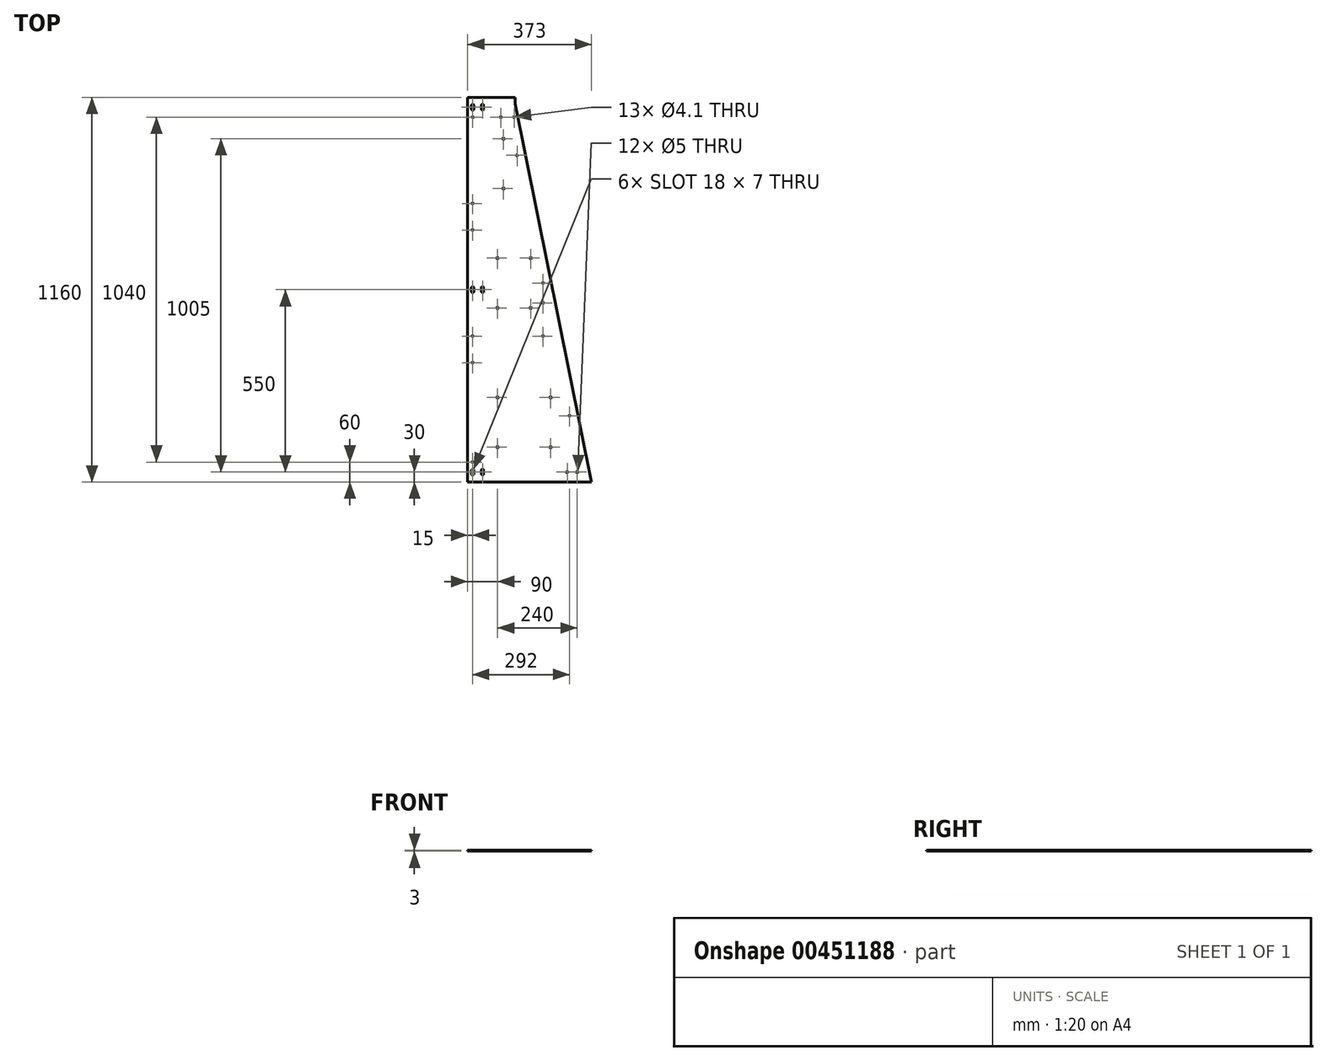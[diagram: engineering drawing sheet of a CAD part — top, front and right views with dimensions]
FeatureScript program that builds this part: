
annotation { "Feature Type Name" : "Feature", "Feature Type Description" : "" }
export const myFeature = defineFeature(function(context is Context, id is Id, definition is map)
    precondition{}
    {
        {
            var Q0;
            Q0=qCreatedBy(makeId("Top.planeOp"),FACE);
            var sketch = newSketch(context, id + "F0", { "sketchPlane" : qUnion([Q0])});
            skLineSegment(sketch, "E0", {"start": v(0, 0) * mm, "end": v(0, 1140) * mm});
            skLineSegment(sketch, "E1", {"start": v(0, 1140) * mm, "end": v(143, 1140) * mm});
            skLineSegment(sketch, "E2", {"start": v(143, 1140) * mm, "end": v(373, 0) * mm});
            skLineSegment(sketch, "E3", {"start": v(373, 0) * mm, "end": v(0, 0) * mm});
            skLineSegment(sketch, "E4", {"start": v(0, 1140) * mm, "end": v(0, 1160) * mm});
            skLineSegment(sketch, "E5", {"start": v(0, 1160) * mm, "end": v(143, 1160) * mm});
            skLineSegment(sketch, "E6", {"start": v(143, 1160) * mm, "end": v(143, 1140) * mm});
            skSolve(sketch);
        }
        {
            var Q0;
            Q0=qSketchRegion(id+"F0",true);
            extrude(context, id + "F1", {"entities" : qUnion([Q0]), "oppositeDirection" : true, "depth" : 3 * mm, "offsetDistance" : 25 * mm});
        }
        {
            var Q0;
            Q0=makeQuery(id+"F1.opExtrude","CAP_FACE",FACE,{"disambiguationData":[OSD([sQuery(id+"F0.wireOp",EDGE,"E0"),sQuery(id+"F0.wireOp",EDGE,"E1"),sQuery(id+"F0.wireOp",EDGE,"E2"),sQuery(id+"F0.wireOp",EDGE,"E3")])],"isStart":true});
            var sketch = newSketch(context, id + "F2", { "sketchPlane" : qUnion([Q0])});
            skCircle(sketch, "E7", {"center": v(90, 105) * mm, "radius": 2.5 * mm});
            skCircle(sketch, "E8", {"center": v(250, 105) * mm, "radius": 2.5 * mm});
            skCircle(sketch, "E9", {"center": v(250, 255) * mm, "radius": 2.5 * mm});
            skCircle(sketch, "E10", {"center": v(90, 255) * mm, "radius": 2.5 * mm});
            skCircle(sketch, "E11", {"center": v(90, 525) * mm, "radius": 2.5 * mm});
            skCircle(sketch, "E12", {"center": v(90, 675) * mm, "radius": 2.5 * mm});
            skCircle(sketch, "E13", {"center": v(190, 525) * mm, "radius": 2.5 * mm});
            skCircle(sketch, "E14", {"center": v(190, 675) * mm, "radius": 2.5 * mm});
            skCircle(sketch, "E15", {"center": v(108, 885) * mm, "radius": 2.5 * mm});
            skCircle(sketch, "E16", {"center": v(108, 1035) * mm, "radius": 2.5 * mm});
            skCircle(sketch, "E17", {"center": v(330, 30) * mm, "radius": 2.5 * mm});
            skCircle(sketch, "E18", {"center": v(300, 30) * mm, "radius": 2.5 * mm});
            skSolve(sketch);
        }
        {
            var Q0;
            Q0=qSketchRegion(id+"F2",true);
            extrude(context, id + "F3", {"entities" : qUnion([Q0]), "operationType" : NewBodyOperationType.REMOVE, "oppositeDirection" : true, "depth" : 25 * mm, "offsetDistance" : 25 * mm});
        }
        {
            var Q0;
            Q0=makeQuery(id+"F1.opExtrude","CAP_FACE",FACE,{"disambiguationData":[OSD([sQuery(id+"F0.wireOp",EDGE,"E0"),sQuery(id+"F0.wireOp",EDGE,"E1"),sQuery(id+"F0.wireOp",EDGE,"E2"),sQuery(id+"F0.wireOp",EDGE,"E3")])],"isStart":true});
            var sketch = newSketch(context, id + "F4", { "sketchPlane" : qUnion([Q0])});
            skLineSegment(sketch, "E19.bottom", {"start": v(18.5, 24.5) * mm, "end": v(11.5, 24.5) * mm, "construction": true});
            skLineSegment(sketch, "E19.top", {"start": v(18.5, 35.5) * mm, "end": v(11.5, 35.5) * mm, "construction": true});
            skLineSegment(sketch, "E19.left", {"start": v(18.5, 24.5) * mm, "end": v(18.5, 35.5) * mm});
            skLineSegment(sketch, "E19.right", {"start": v(11.5, 24.5) * mm, "end": v(11.5, 35.5) * mm});
            skPoint(sketch, "E19.middle", {"position": v(15, 30) * mm});
            skArc(sketch, "E20", {"start": v(18.5, 35.5) * mm, "mid": v(15, 39) * mm, "end": v(11.5, 35.5) * mm});
            skArc(sketch, "E21", {"start": v(11.5, 24.5) * mm, "mid": v(15, 21) * mm, "end": v(18.5, 24.5) * mm});
            skLineSegment(sketch, "E22", {"start": v(81.14, 580) * mm, "end": v(105.06, 580) * mm, "construction": true});
            skLineSegment(sketch, "E23.bottom", {"start": v(48.5, 24.5) * mm, "end": v(41.5, 24.5) * mm, "construction": true});
            skLineSegment(sketch, "E23.top", {"start": v(48.5, 35.5) * mm, "end": v(41.5, 35.5) * mm, "construction": true});
            skLineSegment(sketch, "E23.left", {"start": v(48.5, 24.5) * mm, "end": v(48.5, 35.5) * mm});
            skLineSegment(sketch, "E23.right", {"start": v(41.5, 24.5) * mm, "end": v(41.5, 35.5) * mm});
            skPoint(sketch, "E23.middle", {"position": v(45, 30) * mm});
            skArc(sketch, "E24", {"start": v(48.5, 35.5) * mm, "mid": v(45, 39) * mm, "end": v(41.5, 35.5) * mm});
            skArc(sketch, "E25", {"start": v(41.5, 24.5) * mm, "mid": v(45, 21) * mm, "end": v(48.5, 24.5) * mm});
            skLineSegment(sketch, "E26.bottom", {"start": v(18.5, 574.5) * mm, "end": v(11.5, 574.5) * mm, "construction": true});
            skLineSegment(sketch, "E26.top", {"start": v(18.5, 585.5) * mm, "end": v(11.5, 585.5) * mm, "construction": true});
            skLineSegment(sketch, "E26.left", {"start": v(18.5, 574.5) * mm, "end": v(18.5, 585.5) * mm});
            skLineSegment(sketch, "E26.right", {"start": v(11.5, 574.5) * mm, "end": v(11.5, 585.5) * mm});
            skPoint(sketch, "E26.middle", {"position": v(15, 580) * mm});
            skArc(sketch, "E27", {"start": v(18.5, 585.5) * mm, "mid": v(15, 589) * mm, "end": v(11.5, 585.5) * mm});
            skArc(sketch, "E28", {"start": v(11.5, 574.5) * mm, "mid": v(15, 571) * mm, "end": v(18.5, 574.5) * mm});
            skLineSegment(sketch, "E29.bottom", {"start": v(48.5, 574.5) * mm, "end": v(41.5, 574.5) * mm, "construction": true});
            skLineSegment(sketch, "E29.top", {"start": v(48.5, 585.5) * mm, "end": v(41.5, 585.5) * mm, "construction": true});
            skLineSegment(sketch, "E29.left", {"start": v(48.5, 574.5) * mm, "end": v(48.5, 585.5) * mm});
            skLineSegment(sketch, "E29.right", {"start": v(41.5, 574.5) * mm, "end": v(41.5, 585.5) * mm});
            skPoint(sketch, "E29.middle", {"position": v(45, 580) * mm});
            skArc(sketch, "E30", {"start": v(48.5, 585.5) * mm, "mid": v(45, 589) * mm, "end": v(41.5, 585.5) * mm});
            skArc(sketch, "E31", {"start": v(41.5, 574.5) * mm, "mid": v(45, 571) * mm, "end": v(48.5, 574.5) * mm});
            skLineSegment(sketch, "E32.bottom", {"start": v(18.5, 1124.5) * mm, "end": v(11.5, 1124.5) * mm, "construction": true});
            skLineSegment(sketch, "E32.top", {"start": v(18.5, 1135.5) * mm, "end": v(11.5, 1135.5) * mm, "construction": true});
            skLineSegment(sketch, "E32.left", {"start": v(18.5, 1124.5) * mm, "end": v(18.5, 1135.5) * mm});
            skLineSegment(sketch, "E32.right", {"start": v(11.5, 1124.5) * mm, "end": v(11.5, 1135.5) * mm});
            skPoint(sketch, "E32.middle", {"position": v(15, 1130) * mm});
            skArc(sketch, "E33", {"start": v(18.5, 1135.5) * mm, "mid": v(15, 1139) * mm, "end": v(11.5, 1135.5) * mm});
            skArc(sketch, "E34", {"start": v(11.5, 1124.5) * mm, "mid": v(15, 1121) * mm, "end": v(18.5, 1124.5) * mm});
            skLineSegment(sketch, "E35.bottom", {"start": v(48.5, 1124.5) * mm, "end": v(41.5, 1124.5) * mm, "construction": true});
            skLineSegment(sketch, "E35.top", {"start": v(48.5, 1135.5) * mm, "end": v(41.5, 1135.5) * mm, "construction": true});
            skLineSegment(sketch, "E35.left", {"start": v(48.5, 1124.5) * mm, "end": v(48.5, 1135.5) * mm});
            skLineSegment(sketch, "E35.right", {"start": v(41.5, 1124.5) * mm, "end": v(41.5, 1135.5) * mm});
            skPoint(sketch, "E35.middle", {"position": v(45, 1130) * mm});
            skArc(sketch, "E36", {"start": v(48.5, 1135.5) * mm, "mid": v(45, 1139) * mm, "end": v(41.5, 1135.5) * mm});
            skArc(sketch, "E37", {"start": v(41.5, 1124.5) * mm, "mid": v(45, 1121) * mm, "end": v(48.5, 1124.5) * mm});
            skSolve(sketch);
        }
        {
            var Q0;
            Q0=qSketchRegion(id+"F4",true);
            extrude(context, id + "F5", {"entities" : qUnion([Q0]), "operationType" : NewBodyOperationType.REMOVE, "oppositeDirection" : true, "depth" : 25 * mm, "offsetDistance" : 25 * mm});
        }
        {
            var Q0;
            Q0=qCreatedBy(makeId("Front.planeOp"),FACE);
            cPlane(context, id + "F6", {"entities" : qUnion([Q0]), "cplaneType" : CPlaneType.OFFSET, "offset" : 1122 * mm, "width" : 150 * mm, "height" : 150 * mm});
        }
        {
            var Q0;
            Q0=makeQuery(id+"F1.opExtrude","CAP_FACE",FACE,{"disambiguationData":[OSD([sQuery(id+"F0.wireOp",EDGE,"E0"),sQuery(id+"F0.wireOp",EDGE,"E1"),sQuery(id+"F0.wireOp",EDGE,"E2"),sQuery(id+"F0.wireOp",EDGE,"E3")])],"isStart":true});
            var sketch = newSketch(context, id + "F7", { "sketchPlane" : qUnion([Q0])});
            skCircle(sketch, "E38", {"center": v(15, 60) * mm, "radius": 2.05 * mm});
            skCircle(sketch, "E39", {"center": v(307, 200) * mm, "radius": 2.05 * mm});
            skCircle(sketch, "E40", {"center": v(15, 360) * mm, "radius": 2.05 * mm});
            skCircle(sketch, "E41", {"center": v(15, 440) * mm, "radius": 2.05 * mm});
            skCircle(sketch, "E42", {"center": v(15, 760) * mm, "radius": 2.05 * mm});
            skCircle(sketch, "E43", {"center": v(15, 840) * mm, "radius": 2.05 * mm});
            skCircle(sketch, "E44", {"center": v(15, 1100) * mm, "radius": 2.05 * mm});
            skCircle(sketch, "E45", {"center": v(227, 600) * mm, "radius": 2.05 * mm});
            skCircle(sketch, "E46", {"center": v(149, 985) * mm, "radius": 2.05 * mm});
            skCircle(sketch, "E47", {"center": v(100, 1100) * mm, "radius": 2.05 * mm});
            skCircle(sketch, "E48", {"center": v(140, 1100) * mm, "radius": 2.05 * mm});
            skCircle(sketch, "E49", {"center": v(227, 540) * mm, "radius": 2.05 * mm});
            skCircle(sketch, "E50", {"center": v(227, 440) * mm, "radius": 2.05 * mm});
            skSolve(sketch);
        }
        {
            var Q0;
            Q0=qSketchRegion(id+"F7",true);
            extrude(context, id + "F8", {"entities" : qUnion([Q0]), "operationType" : NewBodyOperationType.REMOVE, "oppositeDirection" : true, "depth" : 25 * mm, "offsetDistance" : 25 * mm});
        }
    });
